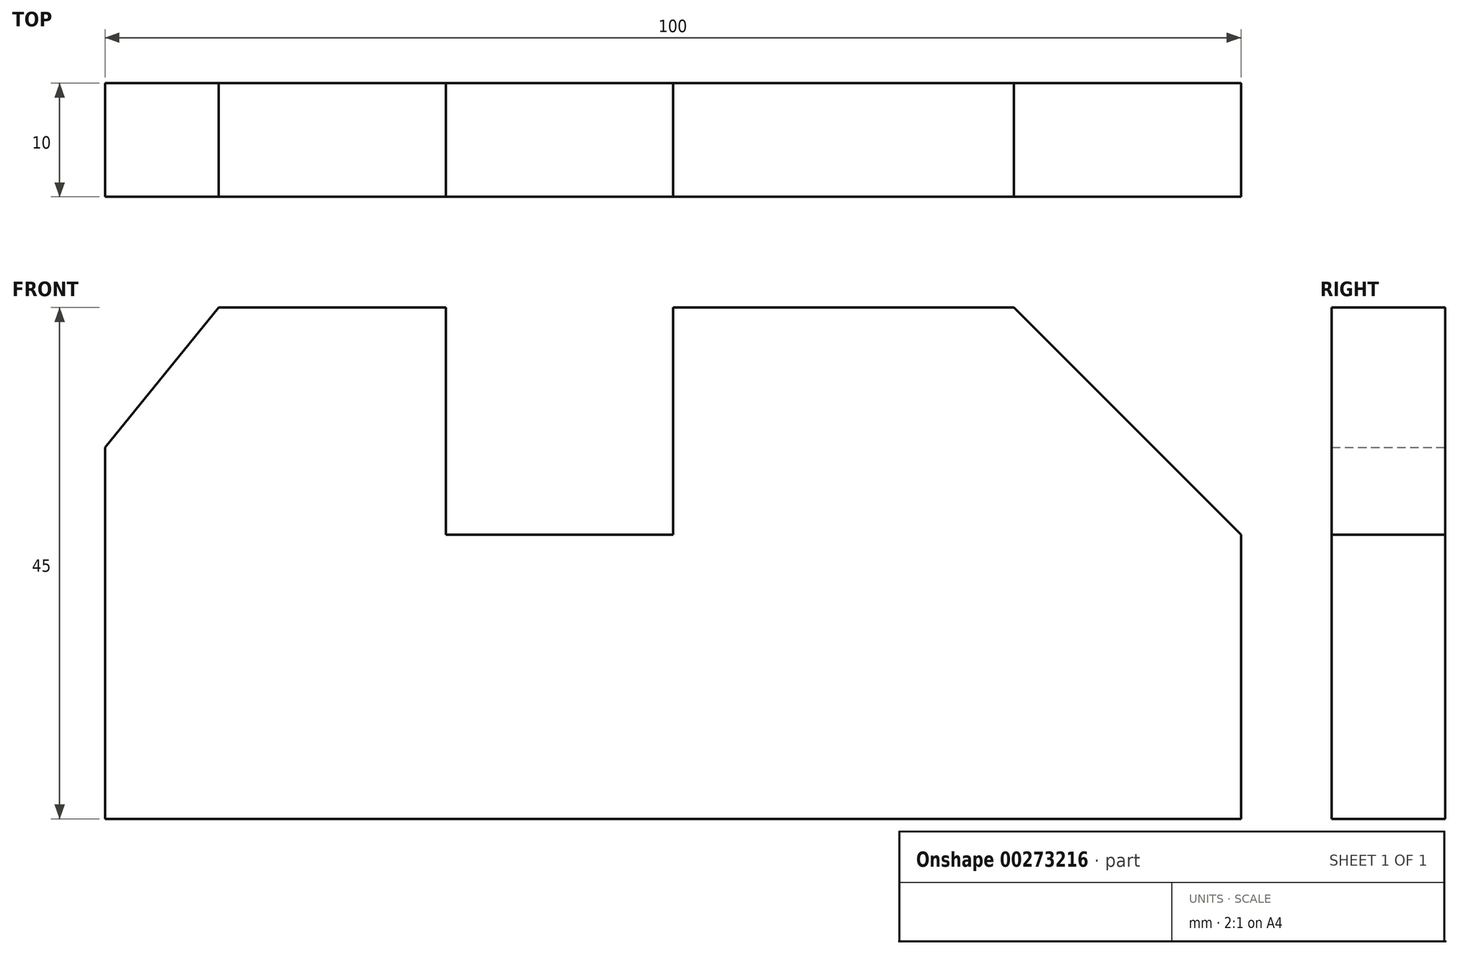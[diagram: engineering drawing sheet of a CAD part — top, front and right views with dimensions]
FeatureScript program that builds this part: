
annotation { "Feature Type Name" : "Feature", "Feature Type Description" : "" }
export const myFeature = defineFeature(function(context is Context, id is Id, definition is map)
    precondition{}
    {
        {
            var Q0;
            Q0=qCreatedBy(makeId("Front.planeOp"),FACE);
            var sketch = newSketch(context, id + "F0", { "sketchPlane" : qUnion([Q0])});
            skLineSegment(sketch, "E0", {"start": v(0, 0) * mm, "end": v(100, 0) * mm});
            skLineSegment(sketch, "E1", {"start": v(100, 0) * mm, "end": v(100, 25) * mm});
            skLineSegment(sketch, "E2", {"start": v(100, 25) * mm, "end": v(80, 45) * mm});
            skLineSegment(sketch, "E3", {"start": v(80, 45) * mm, "end": v(50, 45) * mm});
            skLineSegment(sketch, "E4", {"start": v(50, 45) * mm, "end": v(50, 25) * mm});
            skLineSegment(sketch, "E5", {"start": v(50, 25) * mm, "end": v(30, 25) * mm});
            skLineSegment(sketch, "E6", {"start": v(30, 25) * mm, "end": v(30, 45) * mm});
            skLineSegment(sketch, "E7", {"start": v(30, 45) * mm, "end": v(10, 45) * mm});
            skLineSegment(sketch, "E8", {"start": v(10, 45) * mm, "end": v(0, 32.7) * mm});
            skLineSegment(sketch, "E9", {"start": v(0, 32.7) * mm, "end": v(0, 0) * mm});
            skSolve(sketch);
        }
        {
            var Q0;
            Q0 = qSketchRegion(id + "F0", true);
            extrude(context, id + "F1", {"entities" : qUnion([Q0]), "depth" : 10 * mm});
        }
    });
